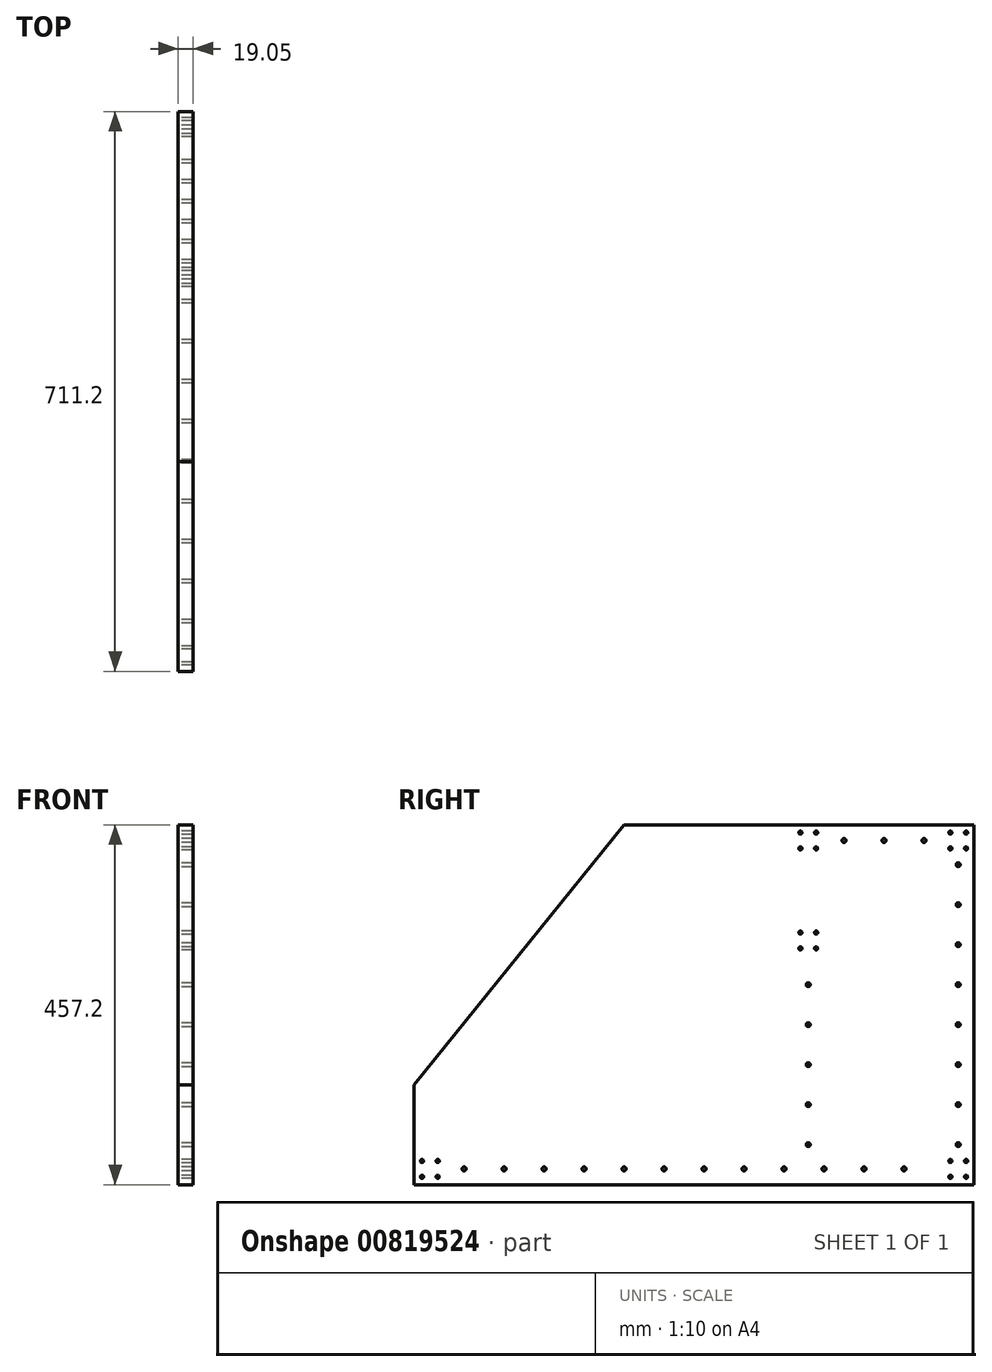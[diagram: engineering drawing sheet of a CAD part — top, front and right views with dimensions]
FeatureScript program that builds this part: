
annotation { "Feature Type Name" : "Feature", "Feature Type Description" : "" }
export const myFeature = defineFeature(function(context is Context, id is Id, definition is map)
    precondition{}
    {
        {
            var Q0;
            Q0=qCreatedBy(makeId("Right.planeOp"),FACE);
            var sketch = newSketch(context, id + "F0", { "sketchPlane" : qUnion([Q0])});
            skLineSegment(sketch, "E0", {"start": v(-355.6, -228.6) * mm, "end": v(355.6, -228.6) * mm});
            skLineSegment(sketch, "E1", {"start": v(355.6, -228.6) * mm, "end": v(355.6, 228.6) * mm});
            skLineSegment(sketch, "E2", {"start": v(355.6, 228.6) * mm, "end": v(-88.9, 228.6) * mm});
            skLineSegment(sketch, "E3", {"start": v(-88.9, 228.6) * mm, "end": v(-355.6, -101.6) * mm});
            skLineSegment(sketch, "E4", {"start": v(-355.6, -101.6) * mm, "end": v(-355.6, -228.6) * mm});
            skCircle(sketch, "E5", {"center": v(-345.6, -198.6) * mm, "radius": 2 * mm});
            skCircle(sketch, "E6", {"center": v(-325.6, -198.6) * mm, "radius": 2 * mm});
            skCircle(sketch, "E7", {"center": v(-325.6, -218.6) * mm, "radius": 2 * mm});
            skCircle(sketch, "E8", {"center": v(-345.6, -218.6) * mm, "radius": 2 * mm});
            skLineSegment(sketch, "E9", {"start": v(-345.6, -198.6) * mm, "end": v(-325.6, -198.6) * mm, "construction": true});
            skLineSegment(sketch, "E10", {"start": v(-325.6, -218.6) * mm, "end": v(-325.6, -198.6) * mm, "construction": true});
            skLineSegment(sketch, "E11", {"start": v(-345.6, -198.6) * mm, "end": v(-345.6, -218.6) * mm, "construction": true});
            skLineSegment(sketch, "E12", {"start": v(-345.6, -218.6) * mm, "end": v(-325.6, -218.6) * mm, "construction": true});
            skLineSegment(sketch, "E13", {"start": v(-345.6, -198.6) * mm, "end": v(-325.6, -218.6) * mm, "construction": true});
            skLineSegment(sketch, "E14", {"start": v(-325.6, -198.6) * mm, "end": v(-335.6, -208.6) * mm, "construction": true});
            skCircle(sketch, "E15", {"center": v(325.6, -198.6) * mm, "radius": 2 * mm});
            skCircle(sketch, "E16", {"center": v(345.6, -198.6) * mm, "radius": 2 * mm});
            skCircle(sketch, "E17", {"center": v(345.6, -218.6) * mm, "radius": 2 * mm});
            skCircle(sketch, "E18", {"center": v(325.6, -218.6) * mm, "radius": 2 * mm});
            skLineSegment(sketch, "E19", {"start": v(325.6, -198.6) * mm, "end": v(345.6, -198.6) * mm, "construction": true});
            skLineSegment(sketch, "E20", {"start": v(345.6, -218.6) * mm, "end": v(345.6, -198.6) * mm, "construction": true});
            skLineSegment(sketch, "E21", {"start": v(325.6, -198.6) * mm, "end": v(325.6, -218.6) * mm, "construction": true});
            skLineSegment(sketch, "E22", {"start": v(325.6, -218.6) * mm, "end": v(345.6, -218.6) * mm, "construction": true});
            skLineSegment(sketch, "E23", {"start": v(325.6, -198.6) * mm, "end": v(345.6, -218.6) * mm, "construction": true});
            skLineSegment(sketch, "E24", {"start": v(345.6, -198.6) * mm, "end": v(335.6, -208.6) * mm, "construction": true});
            skCircle(sketch, "E25", {"center": v(325.6, 218.6) * mm, "radius": 2 * mm});
            skCircle(sketch, "E26", {"center": v(345.6, 218.6) * mm, "radius": 2 * mm});
            skCircle(sketch, "E27", {"center": v(345.6, 198.6) * mm, "radius": 2 * mm});
            skCircle(sketch, "E28", {"center": v(325.6, 198.6) * mm, "radius": 2 * mm});
            skLineSegment(sketch, "E29", {"start": v(325.6, 218.6) * mm, "end": v(345.6, 218.6) * mm, "construction": true});
            skLineSegment(sketch, "E30", {"start": v(345.6, 198.6) * mm, "end": v(345.6, 218.6) * mm, "construction": true});
            skLineSegment(sketch, "E31", {"start": v(325.6, 218.6) * mm, "end": v(325.6, 198.6) * mm, "construction": true});
            skLineSegment(sketch, "E32", {"start": v(325.6, 198.6) * mm, "end": v(345.6, 198.6) * mm, "construction": true});
            skLineSegment(sketch, "E33", {"start": v(325.6, 218.6) * mm, "end": v(345.6, 198.6) * mm, "construction": true});
            skLineSegment(sketch, "E34", {"start": v(345.6, 218.6) * mm, "end": v(335.6, 208.6) * mm, "construction": true});
            skCircle(sketch, "E35", {"center": v(135.1, 218.6) * mm, "radius": 2 * mm});
            skCircle(sketch, "E36", {"center": v(155.1, 218.6) * mm, "radius": 2 * mm});
            skCircle(sketch, "E37", {"center": v(155.1, 198.6) * mm, "radius": 2 * mm});
            skCircle(sketch, "E38", {"center": v(135.1, 198.6) * mm, "radius": 2 * mm});
            skLineSegment(sketch, "E39", {"start": v(135.1, 218.6) * mm, "end": v(155.1, 218.6) * mm, "construction": true});
            skLineSegment(sketch, "E40", {"start": v(155.1, 198.6) * mm, "end": v(155.1, 218.6) * mm, "construction": true});
            skLineSegment(sketch, "E41", {"start": v(135.1, 218.6) * mm, "end": v(135.1, 198.6) * mm, "construction": true});
            skLineSegment(sketch, "E42", {"start": v(135.1, 198.6) * mm, "end": v(155.1, 198.6) * mm, "construction": true});
            skLineSegment(sketch, "E43", {"start": v(135.1, 218.6) * mm, "end": v(155.1, 198.6) * mm, "construction": true});
            skLineSegment(sketch, "E44", {"start": v(155.1, 218.6) * mm, "end": v(145.1, 208.6) * mm, "construction": true});
            skCircle(sketch, "E45", {"center": v(135.1, 91.6) * mm, "radius": 2 * mm});
            skCircle(sketch, "E46", {"center": v(155.1, 91.6) * mm, "radius": 2 * mm});
            skCircle(sketch, "E47", {"center": v(155.1, 71.6) * mm, "radius": 2 * mm});
            skCircle(sketch, "E48", {"center": v(135.1, 71.6) * mm, "radius": 2 * mm});
            skLineSegment(sketch, "E49", {"start": v(135.1, 91.6) * mm, "end": v(155.1, 91.6) * mm, "construction": true});
            skLineSegment(sketch, "E50", {"start": v(155.1, 71.6) * mm, "end": v(155.1, 91.6) * mm, "construction": true});
            skLineSegment(sketch, "E51", {"start": v(135.1, 91.6) * mm, "end": v(135.1, 71.6) * mm, "construction": true});
            skLineSegment(sketch, "E52", {"start": v(135.1, 71.6) * mm, "end": v(155.1, 71.6) * mm, "construction": true});
            skLineSegment(sketch, "E53", {"start": v(135.1, 91.6) * mm, "end": v(155.1, 71.6) * mm, "construction": true});
            skLineSegment(sketch, "E54", {"start": v(155.1, 91.6) * mm, "end": v(145.1, 81.6) * mm, "construction": true});
            skLineSegment(sketch, "E55", {"start": v(355.6, 0) * mm, "end": v(-355.6, 0) * mm, "construction": true});
            skLineSegment(sketch, "E56", {"start": v(0, -228.6) * mm, "end": v(0, 228.6) * mm, "construction": true});
            skCircle(sketch, "E57", {"center": v(-292.1, -208.6) * mm, "radius": 2.5 * mm});
            skCircle(sketch, "E58.1.0.0", {"center": v(-241.3, -208.6) * mm, "radius": 2.5 * mm});
            skCircle(sketch, "E58.2.0.0", {"center": v(-190.5, -208.6) * mm, "radius": 2.5 * mm});
            skCircle(sketch, "E58.3.0.0", {"center": v(-139.7, -208.6) * mm, "radius": 2.5 * mm});
            skCircle(sketch, "E58.4.0.0", {"center": v(-88.9, -208.6) * mm, "radius": 2.5 * mm});
            skCircle(sketch, "E58.5.0.0", {"center": v(-38.1, -208.6) * mm, "radius": 2.5 * mm});
            skCircle(sketch, "E58.6.0.0", {"center": v(12.7, -208.6) * mm, "radius": 2.5 * mm});
            skCircle(sketch, "E58.7.0.0", {"center": v(63.5, -208.6) * mm, "radius": 2.5 * mm});
            skCircle(sketch, "E58.8.0.0", {"center": v(114.3, -208.6) * mm, "radius": 2.5 * mm});
            skLineSegment(sketch, "E58.direction1", {"start": v(-292.1, -208.6) * mm, "end": v(-241.3, -208.6) * mm, "construction": true});
            skCircle(sketch, "E59", {"center": v(145.1, -177.8) * mm, "radius": 2.5 * mm});
            skCircle(sketch, "E60.0.1.0", {"center": v(145.1, -127) * mm, "radius": 2.5 * mm});
            skCircle(sketch, "E60.0.2.0", {"center": v(145.1, -76.2) * mm, "radius": 2.5 * mm});
            skLineSegment(sketch, "E60.direction1", {"start": v(119.35, -177.8) * mm, "end": v(145.1, -177.8) * mm, "construction": true});
            skLineSegment(sketch, "E60.direction2", {"start": v(145.1, -177.8) * mm, "end": v(145.1, -127) * mm, "construction": true});
            skCircle(sketch, "E61", {"center": v(335.6, -177.8) * mm, "radius": 2.5 * mm});
            skCircle(sketch, "E62.0.1.0", {"center": v(335.6, -127) * mm, "radius": 2.5 * mm});
            skCircle(sketch, "E62.0.2.0", {"center": v(335.6, -76.2) * mm, "radius": 2.5 * mm});
            skCircle(sketch, "E62.0.3.0", {"center": v(335.6, -25.4) * mm, "radius": 2.5 * mm});
            skCircle(sketch, "E62.0.4.0", {"center": v(335.6, 25.4) * mm, "radius": 2.5 * mm});
            skLineSegment(sketch, "E62.direction1", {"start": v(335.6, -177.8) * mm, "end": v(350.6, -177.8) * mm, "construction": true});
            skLineSegment(sketch, "E62.direction2", {"start": v(335.6, -177.8) * mm, "end": v(335.6, -127) * mm, "construction": true});
            skCircle(sketch, "E63.0.9.0", {"center": v(165.1, -208.6) * mm, "radius": 2.5 * mm});
            skCircle(sketch, "E64.0.10.0", {"center": v(215.9, -208.6) * mm, "radius": 2.5 * mm});
            skCircle(sketch, "E64.0.11.0", {"center": v(266.7, -208.6) * mm, "radius": 2.5 * mm});
            skCircle(sketch, "E65.0.0.3", {"center": v(145.1, -25.4) * mm, "radius": 2.5 * mm});
            skCircle(sketch, "E66.0.0.5", {"center": v(335.6, 76.2) * mm, "radius": 2.5 * mm});
            skCircle(sketch, "E67.0.0.4", {"center": v(145.1, 25.4) * mm, "radius": 2.5 * mm});
            skCircle(sketch, "E68.0.0.6", {"center": v(335.6, 127) * mm, "radius": 2.5 * mm});
            skCircle(sketch, "E69", {"center": v(292.1, 208.6) * mm, "radius": 2.5 * mm});
            skCircle(sketch, "E70.1.0.0", {"center": v(241.3, 208.6) * mm, "radius": 2.5 * mm});
            skCircle(sketch, "E70.2.0.0", {"center": v(190.5, 208.6) * mm, "radius": 2.5 * mm});
            skLineSegment(sketch, "E70.direction1", {"start": v(292.1, 208.6) * mm, "end": v(241.3, 208.6) * mm, "construction": true});
            skCircle(sketch, "E71.0.0.7", {"center": v(335.6, 177.8) * mm, "radius": 2.5 * mm});
            skSolve(sketch);
        }
        {
            var Q0;
            Q0=makeQuery(id+"F0.imprint","IMPRINT",FACE,{"disambiguationData":[TD([[makeQuery(id+"F0.imprint","IMPRINT",EDGE,{"derivedFrom":sQuery(id+"F0.wireOp",EDGE,"E0")}),1.0]])]});
            extrude(context, id + "F1", {"entities" : qUnion([Q0]), "depth" : 19.05 * mm, "offsetDistance" : 25.4 * mm});
        }
    });
